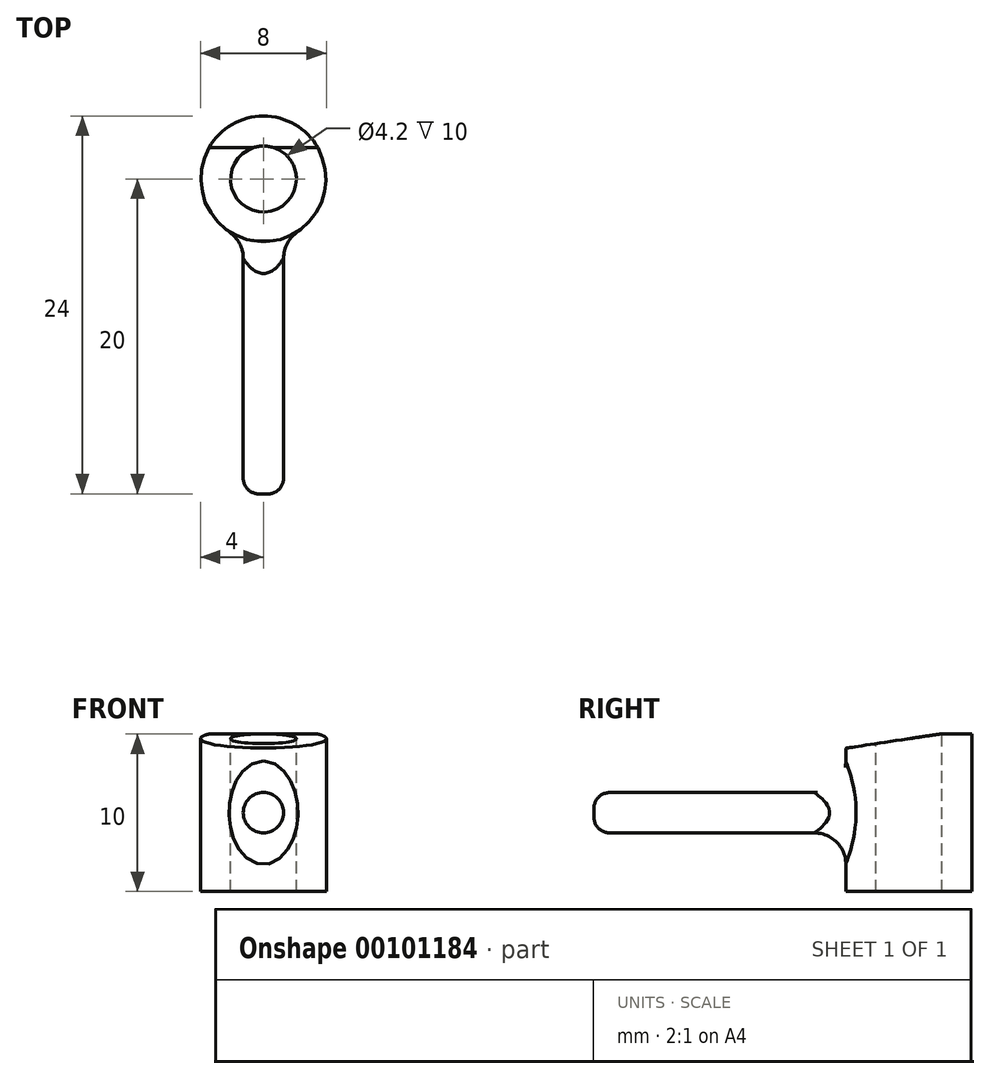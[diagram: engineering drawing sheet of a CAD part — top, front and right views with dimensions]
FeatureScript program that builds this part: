
annotation { "Feature Type Name" : "Feature", "Feature Type Description" : "" }
export const myFeature = defineFeature(function(context is Context, id is Id, definition is map)
    precondition{}
    {
        {
            var Q0;
            Q0=qCreatedBy(makeId("Front.planeOp"),FACE);
            var sketch = newSketch(context, id + "F0", { "sketchPlane" : qUnion([Q0])});
            skCircle(sketch, "E0", {"center": v(0, 0) * mm, "radius": 1.28 * mm});
            skSolve(sketch);
        }
        {
            var Q0;
            Q0 = qSketchRegion(id + "F0", true);
            extrude(context, id + "F1", {"entities" : qUnion([Q0]), "depth" : 20 * mm});
        }
        {
            var Q0;
            Q0=qCreatedBy(makeId("Top.planeOp"),FACE);
            var sketch = newSketch(context, id + "F2", { "sketchPlane" : qUnion([Q0])});
            skCircle(sketch, "E1", {"center": v(0, 0) * mm, "radius": 4 * mm});
            skSolve(sketch);
        }
        {
            var Q0;
            Q0=makeQuery(id+"F2.imprint","IMPRINT",FACE,{"disambiguationData":[TD([[makeQuery(id+"F2.imprint","IMPRINT",EDGE,{"derivedFrom":sQuery(id+"F2.wireOp",EDGE,"E1")}),1.0]])]});
            var Q1;
            Q1=sQuery(id+"F2.wireOp",EDGE,"E1");
            extrude(context, id + "F3", {"entities" : qUnion([Q0]), "operationType" : NewBodyOperationType.ADD, "surfaceEntities" : qUnion([Q1]), "endBound" : BoundingType.SYMMETRIC, "depth" : 10 * mm});
        }
        {
            var Q0;
            Q0=qCreatedBy(makeId("Right.planeOp"),FACE);
            var sketch = newSketch(context, id + "F4", { "sketchPlane" : qUnion([Q0])});
            skLineSegment(sketch, "E2", {"start": v(2, 5) * mm, "end": v(-6, 3.8) * mm});
            skLineSegment(sketch, "E3", {"start": v(2, 5) * mm, "end": v(6, 5) * mm});
            skLineSegment(sketch, "E4", {"start": v(-6, 3.8) * mm, "end": v(-6, 10.39) * mm});
            skLineSegment(sketch, "E5", {"start": v(-6, 10.39) * mm, "end": v(2, 5) * mm});
            skSolve(sketch);
        }
        {
            var Q0;
            Q0=makeQuery(id+"F4.imprint","IMPRINT",FACE,{"disambiguationData":[TD([[makeQuery(id+"F4.imprint","IMPRINT",EDGE,{"derivedFrom":sQuery(id+"F4.wireOp",EDGE,"E2")}),-1.0]])]});
            var Q1;
            Q1=sQuery(id+"F4.wireOp",EDGE,"E4");
            var Q2;
            Q2=sQuery(id+"F4.wireOp",EDGE,"E5");
            var Q3;
            Q3=sQuery(id+"F4.wireOp",EDGE,"E2");
            extrude(context, id + "F5", {"entities" : qUnion([Q0]), "operationType" : NewBodyOperationType.REMOVE, "surfaceEntities" : qUnion([Q1, Q2, Q3]), "endBound" : BoundingType.SYMMETRIC, "depth" : 25 * mm});
        }
        {
            var Q0;
            Q0=qCreatedBy(makeId("Top.planeOp"),FACE);
            var sketch = newSketch(context, id + "F6", { "sketchPlane" : qUnion([Q0])});
            skCircle(sketch, "E6", {"center": v(0, 0) * mm, "radius": 2.1 * mm});
            skSolve(sketch);
        }
        {
            var Q0;
            Q0 = qSketchRegion(id + "F6", true);
            extrude(context, id + "F7", {"entities" : qUnion([Q0]), "operationType" : NewBodyOperationType.REMOVE, "endBound" : BoundingType.SYMMETRIC, "oppositeDirection" : true, "depth" : 25 * mm});
        }
        {
            var Q0;
            Q0=makeQuery(id+"F3.boolean.opBoolean","INTERSECT",EDGE,{"derivedFrom":[makeQuery(id+"F1.opExtrude","SWEPT_FACE",FACE,{"disambiguationData":[OSD([sQuery(id+"F0.wireOp",EDGE,"E0")])]}),makeQuery(id+"F3.opExtrude","SWEPT_FACE",FACE,{"disambiguationData":[OSD([sQuery(id+"F2.wireOp",EDGE,"E1")])]})]});
            fillet(context, id + "F8", {"entities" : qUnion([Q0]), "radius" : 2 * mm, "tangentPropagation" : true, "allowEdgeOverflow" : false});
        }
        {
            var Q0;
            Q0=makeQuery(id+"F1.opExtrude","CAP_EDGE",EDGE,{"disambiguationData":[OSD([sQuery(id+"F0.wireOp",EDGE,"E0")])],"isStart":false});
            fillet(context, id + "F9", {"entities" : qUnion([Q0]), "radius" : 1 * mm, "tangentPropagation" : true, "allowEdgeOverflow" : false});
        }
    });
